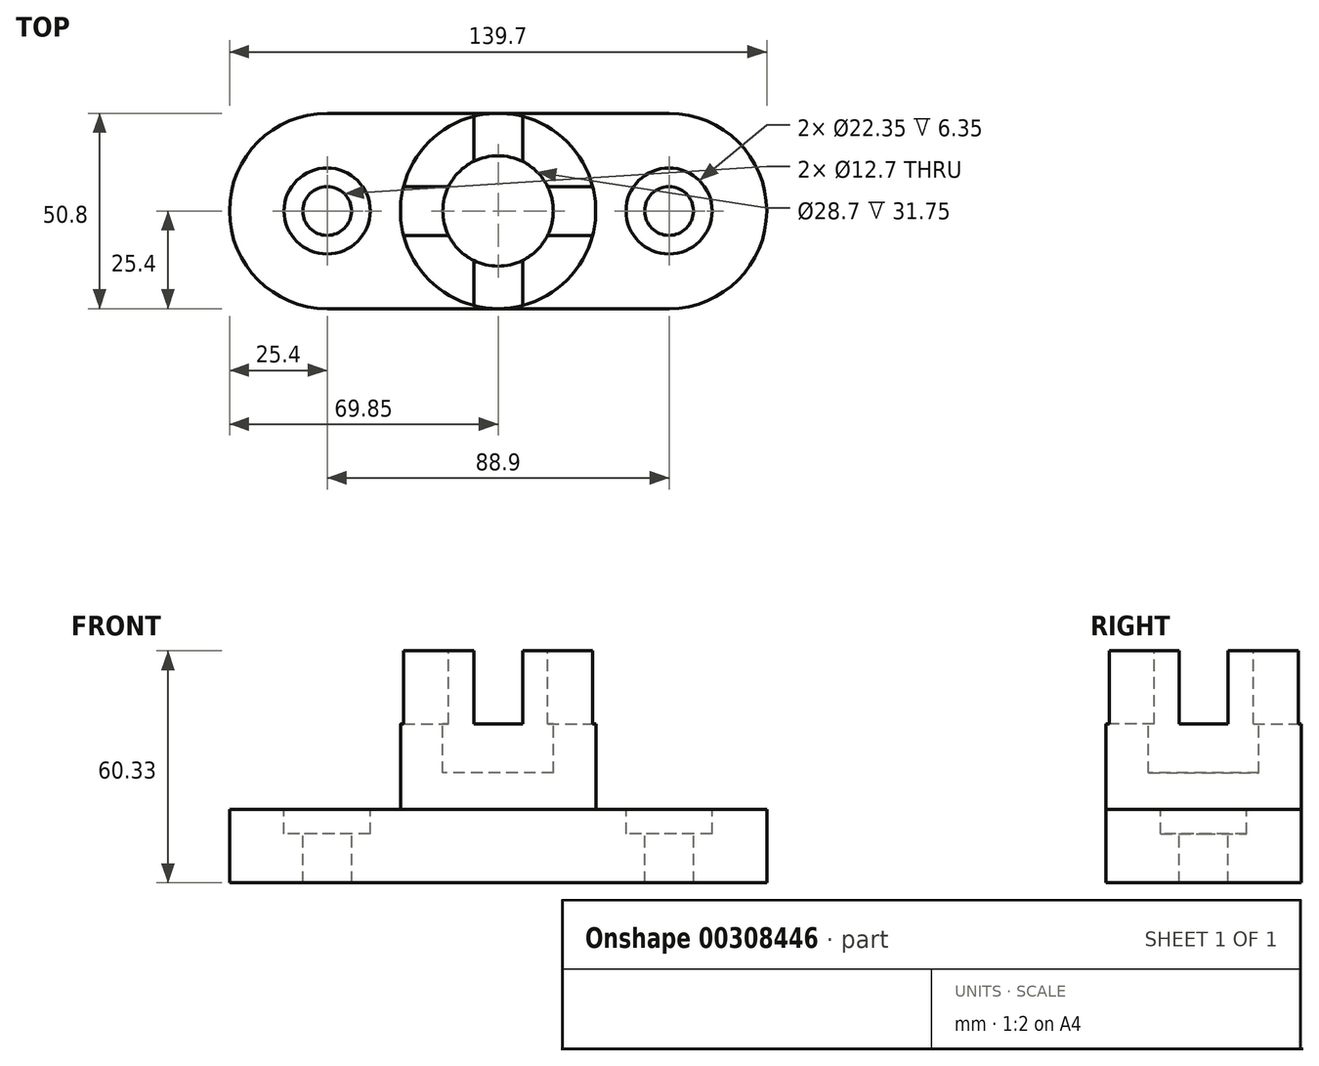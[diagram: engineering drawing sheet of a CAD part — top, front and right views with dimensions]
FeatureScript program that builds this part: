
annotation { "Feature Type Name" : "Feature", "Feature Type Description" : "" }
export const myFeature = defineFeature(function(context is Context, id is Id, definition is map)
    precondition{}
    {
        {
            var Q0;
            Q0=qCreatedBy(makeId("Top.planeOp"),FACE);
            var sketch = newSketch(context, id + "F0", { "sketchPlane" : qUnion([Q0])});
            skLineSegment(sketch, "E0", {"start": v(0, 0) * mm, "end": v(88.9, 0) * mm, "construction": true});
            skArc(sketch, "E1.0.startCap", {"start": v(0, -25.4) * mm, "mid": v(-25.4, 0) * mm, "end": v(0, 25.4) * mm});
            skArc(sketch, "E1.0.endCap", {"start": v(88.9, 25.4) * mm, "mid": v(114.3, 0) * mm, "end": v(88.9, -25.4) * mm});
            skLineSegment(sketch, "E1.0.left", {"start": v(0, 25.4) * mm, "end": v(88.9, 25.4) * mm});
            skLineSegment(sketch, "E1.0.right", {"start": v(0, -25.4) * mm, "end": v(88.9, -25.4) * mm});
            skSolve(sketch);
        }
        {
            var Q0;
            Q0 = qSketchRegion(id + "F0", true);
            extrude(context, id + "F1", {"entities" : qUnion([Q0]), "endBound" : BoundingType.SYMMETRIC, "depth" : 19.05 * mm});
        }
        {
            var Q0;
            Q0=makeQuery(id+"F1.opExtrude","CAP_FACE",FACE,{"disambiguationData":[OSD([sQuery(id+"F0.wireOp",EDGE,"E1.0.startCap"),sQuery(id+"F0.wireOp",EDGE,"E1.0.endCap"),sQuery(id+"F0.wireOp",EDGE,"E1.0.left"),sQuery(id+"F0.wireOp",EDGE,"E1.0.right")])],"isStart":false});
            var sketch = newSketch(context, id + "F2", { "sketchPlane" : qUnion([Q0])});
            skCircle(sketch, "E2", {"center": v(0, 0) * mm, "radius": 11.18 * mm});
            skCircle(sketch, "E3", {"center": v(88.9, 0) * mm, "radius": 11.18 * mm});
            skSolve(sketch);
        }
        {
            var Q0;
            Q0 = qSketchRegion(id + "F2", true);
            extrude(context, id + "F3", {"entities" : qUnion([Q0]), "operationType" : NewBodyOperationType.REMOVE, "oppositeDirection" : true, "depth" : 6.35 * mm});
        }
        {
            var Q0;
            Q0=makeQuery(id+"F1.opExtrude","CAP_FACE",FACE,{"disambiguationData":[OSD([sQuery(id+"F0.wireOp",EDGE,"E1.0.startCap"),sQuery(id+"F0.wireOp",EDGE,"E1.0.endCap"),sQuery(id+"F0.wireOp",EDGE,"E1.0.left"),sQuery(id+"F0.wireOp",EDGE,"E1.0.right")])],"isStart":false});
            var sketch = newSketch(context, id + "F4", { "sketchPlane" : qUnion([Q0])});
            skCircle(sketch, "E4", {"center": v(0, 0) * mm, "radius": 6.35 * mm});
            skCircle(sketch, "E5", {"center": v(88.9, 0) * mm, "radius": 6.35 * mm});
            skSolve(sketch);
        }
        {
            var Q0;
            Q0 = qSketchRegion(id + "F4", true);
            extrude(context, id + "F5", {"entities" : qUnion([Q0]), "operationType" : NewBodyOperationType.REMOVE, "oppositeDirection" : true, "depth" : 19.05 * mm});
        }
        {
            var Q0;
            Q0=qCreatedBy(makeId("Top.planeOp"),FACE);
            var sketch = newSketch(context, id + "F6", { "sketchPlane" : qUnion([Q0])});
            skCircle(sketch, "E6", {"center": v(44.45, 0) * mm, "radius": 25.4 * mm});
            skSolve(sketch);
        }
        {
            var Q0;
            Q0 = qSketchRegion(id + "F6", true);
            extrude(context, id + "F7", {"entities" : qUnion([Q0]), "operationType" : NewBodyOperationType.ADD, "depth" : 50.8 * mm});
        }
        {
            var Q0;
            Q0=makeQuery(id+"F7.opExtrude","CAP_FACE",FACE,{"disambiguationData":[OSD([sQuery(id+"F6.wireOp",EDGE,"E6")])],"isStart":false});
            var sketch = newSketch(context, id + "F8", { "sketchPlane" : qUnion([Q0])});
            skCircle(sketch, "E7", {"center": v(44.45, 0) * mm, "radius": 14.35 * mm});
            skSolve(sketch);
        }
        {
            var Q0;
            Q0 = qSketchRegion(id + "F8", true);
            extrude(context, id + "F9", {"entities" : qUnion([Q0]), "operationType" : NewBodyOperationType.REMOVE, "oppositeDirection" : true, "depth" : 31.75 * mm});
        }
        {
            var Q0;
            Q0=makeQuery(id+"F7.opExtrude","CAP_FACE",FACE,{"disambiguationData":[OSD([sQuery(id+"F6.wireOp",EDGE,"E6")])],"isStart":false});
            var sketch = newSketch(context, id + "F10", { "sketchPlane" : qUnion([Q0])});
            skLineSegment(sketch, "E8", {"start": v(44.45, -25.4) * mm, "end": v(44.45, 0) * mm, "construction": true});
            skLineSegment(sketch, "E9", {"start": v(19.05, 0) * mm, "end": v(44.45, 0) * mm, "construction": true});
            skLineSegment(sketch, "E10", {"start": v(19.86, 6.35) * mm, "end": v(31.58, 6.35) * mm});
            skLineSegment(sketch, "E11", {"start": v(19.86, -6.35) * mm, "end": v(31.58, -6.35) * mm});
            skLineSegment(sketch, "E12", {"start": v(38.1, -12.87) * mm, "end": v(38.1, -24.6) * mm});
            skLineSegment(sketch, "E13", {"start": v(50.8, -12.87) * mm, "end": v(50.8, -24.6) * mm});
            skLineSegment(sketch, "E14", {"start": v(57.32, -6.35) * mm, "end": v(69.04, -6.35) * mm});
            skLineSegment(sketch, "E15", {"start": v(57.32, 6.35) * mm, "end": v(69.04, 6.35) * mm});
            skLineSegment(sketch, "E16", {"start": v(50.8, 12.87) * mm, "end": v(50.8, 24.6) * mm});
            skLineSegment(sketch, "E17", {"start": v(38.1, 12.87) * mm, "end": v(38.1, 24.6) * mm});
            skArc(sketch, "E18", {"start": v(50.8, 24.6) * mm, "mid": v(44.45, 25.4) * mm, "end": v(38.1, 24.6) * mm});
            skArc(sketch, "E19", {"start": v(50.8, 12.87) * mm, "mid": v(44.45, 14.35) * mm, "end": v(38.1, 12.87) * mm});
            skArc(sketch, "E20", {"start": v(19.86, 6.35) * mm, "mid": v(19.05, 0) * mm, "end": v(19.86, -6.35) * mm});
            skArc(sketch, "E21", {"start": v(31.58, 6.35) * mm, "mid": v(30.1, 0) * mm, "end": v(31.58, -6.35) * mm});
            skArc(sketch, "E22", {"start": v(57.32, -6.35) * mm, "mid": v(58.8, 0) * mm, "end": v(57.32, 6.35) * mm});
            skArc(sketch, "E23", {"start": v(69.04, -6.35) * mm, "mid": v(69.85, 0) * mm, "end": v(69.04, 6.35) * mm});
            skArc(sketch, "E24", {"start": v(38.1, -12.87) * mm, "mid": v(44.45, -14.35) * mm, "end": v(50.8, -12.87) * mm});
            skArc(sketch, "E25", {"start": v(38.1, -24.6) * mm, "mid": v(44.45, -25.4) * mm, "end": v(50.8, -24.6) * mm});
            skSolve(sketch);
        }
        {
            var Q0;
            Q0 = qSketchRegion(id + "F10", true);
            extrude(context, id + "F11", {"entities" : qUnion([Q0]), "operationType" : NewBodyOperationType.REMOVE, "oppositeDirection" : true, "depth" : 19.05 * mm});
        }
        {
            var Q0;
            Q0 = qSketchRegion(id + "F10", true);
            extrude(context, id + "F12", {"entities" : qUnion([Q0]), "operationType" : NewBodyOperationType.REMOVE, "oppositeDirection" : true, "depth" : 19.05 * mm});
        }
    });
